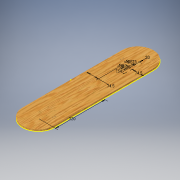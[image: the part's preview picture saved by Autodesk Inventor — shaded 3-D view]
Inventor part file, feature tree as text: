
AUTODESK INVENTOR PART (.ipt)
format: ipt  version: 2019 (Build 230136000, 136)  size: 168,960 bytes
history: native  units: mm
features: sketch x5, hole x4, other x1, extrude x1
ambient origin geometry x8: Origin, YZ Plane, XZ Plane, XY Plane, X Axis, Y Axis, Z Axis, Center Point
bodies: Body1 (feature_tree)
feature tree (11):
  other  "ソリッド1"
  sketch  "スケッチ1"
  extrude  "押し出し1"  Depth=270.0mm
  sketch  "スケッチ4"
  hole  "穴2"  [1 undecoded]
  hole  "穴3"  [1 undecoded]
  hole  "穴4"  [1 undecoded]
  hole  "穴5"  [1 undecoded]
  sketch  "スケッチ2"
  sketch  "スケッチ6"
  sketch  "スケッチ7"
note: 4 required parameter values undecoded (feature->parameter linkage not recoverable at this tier; creation-order binding heuristic only, values carry confidence <= 0.55)
